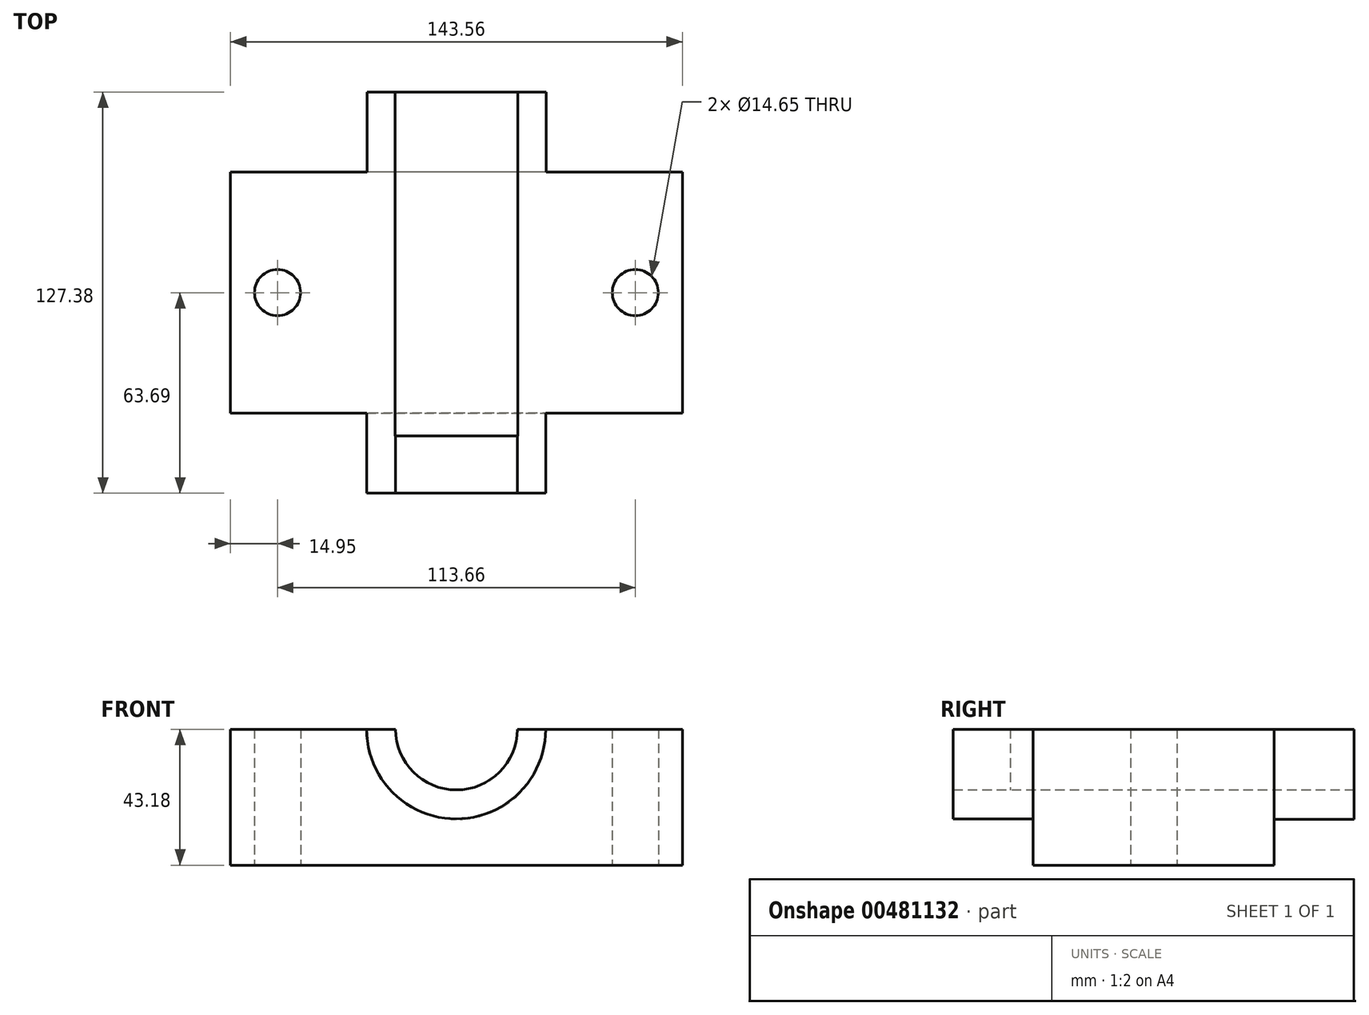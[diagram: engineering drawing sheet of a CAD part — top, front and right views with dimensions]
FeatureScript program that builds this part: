
annotation { "Feature Type Name" : "Feature", "Feature Type Description" : "" }
export const myFeature = defineFeature(function(context is Context, id is Id, definition is map)
    precondition{}
    {
        {
            var Q0;
            Q0=qCreatedBy(makeId("Top.planeOp"),FACE);
            var sketch = newSketch(context, id + "F0", { "sketchPlane" : qUnion([Q0])});
            skLineSegment(sketch, "E0.bottom", {"start": v(71.78, -38.29) * mm, "end": v(-71.78, -38.29) * mm});
            skLineSegment(sketch, "E0.top", {"start": v(71.78, 38.29) * mm, "end": v(-71.78, 38.29) * mm});
            skLineSegment(sketch, "E0.left", {"start": v(71.78, -38.29) * mm, "end": v(71.78, 38.29) * mm});
            skLineSegment(sketch, "E0.right", {"start": v(-71.78, -38.29) * mm, "end": v(-71.78, 38.29) * mm});
            skPoint(sketch, "E0.middle", {"position": v(0, 0) * mm});
            skCircle(sketch, "E1", {"center": v(-56.83, 0) * mm, "radius": 7.33 * mm});
            skCircle(sketch, "E2", {"center": v(56.83, 0) * mm, "radius": 7.33 * mm});
            skSolve(sketch);
        }
        {
            var Q0;
            Q0 = qSketchRegion(id + "F0", true);
            extrude(context, id + "F1", {"entities" : qUnion([Q0]), "depth" : 43.18 * mm});
        }
        {
            var Q0;
            Q0=makeQuery(id+"F1.opExtrude","SWEPT_FACE",FACE,{"disambiguationData":[OSD([sQuery(id+"F0.wireOp",EDGE,"E0.bottom")])]});
            var sketch = newSketch(context, id + "F2", { "sketchPlane" : qUnion([Q0])});
            skArc(sketch, "E3", {"start": v(-28.53, 43.18) * mm, "mid": v(-0.1, 14.7) * mm, "end": v(28.33, 43.18) * mm});
            skArc(sketch, "E4", {"start": v(-19.34, 43.18) * mm, "mid": v(0, 23.9) * mm, "end": v(19.34, 43.18) * mm});
            skSolve(sketch);
        }
        {
            var Q0;
            Q0 = qSketchRegion(id + "F2", true);
            var Q1;
            {var subQ0=sQuery(id+"F2.wireOp",EDGE,"E3");Q1=makeQuery(id+"F2.imprint","IMPRINT",FACE,{"disambiguationData":[TD([[makeQuery(id+"F2.imprint","IMPRINT",EDGE,{"derivedFrom":subQ0}),1.0]])]});}
            extrude(context, id + "F3", {"entities" : qUnion([Q0, Q1]), "operationType" : NewBodyOperationType.ADD, "depth" : 25.4 * mm});
        }
        {
            var Q0;
            Q0=makeQuery(id+"F1.opExtrude","SWEPT_FACE",FACE,{"disambiguationData":[OSD([sQuery(id+"F0.wireOp",EDGE,"E0.top")])]});
            var sketch = newSketch(context, id + "F4", { "sketchPlane" : qUnion([Q0])});
            skArc(sketch, "E5", {"start": v(-28.53, 43.18) * mm, "mid": v(-0.1, 14.54) * mm, "end": v(28.33, 43.18) * mm});
            skArc(sketch, "E6", {"start": v(-19.54, 43.18) * mm, "mid": v(0, 23.82) * mm, "end": v(19.54, 43.18) * mm});
            skSolve(sketch);
        }
        {
            var Q0;
            {var subQ0=sQuery(id+"F4.wireOp",EDGE,"E5");Q0=makeQuery(id+"F4.imprint","IMPRINT",FACE,{"disambiguationData":[TD([[makeQuery(id+"F4.imprint","IMPRINT",EDGE,{"derivedFrom":subQ0}),1.0]])]});}
            extrude(context, id + "F5", {"entities" : qUnion([Q0]), "operationType" : NewBodyOperationType.ADD, "depth" : 25.4 * mm});
        }
        {
            var Q0;
            {var subQ0=sQuery(id+"F4.wireOp",EDGE,"E6");var subQ5=sQuery(id+"F0.wireOp",EDGE,"E0.top");Q0=makeQuery(id+"F5.boolean.opBoolean","SPLIT",FACE,{"disambiguationData":[TD([makeQuery(id+"F5.opExtrude","SWEPT_FACE",FACE,{"disambiguationData":[OSD([subQ0])]})])],"derivedFrom":makeQuery(id+"F1.opExtrude","SWEPT_FACE",FACE,{"disambiguationData":[OSD([subQ5])]})});}
            extrude(context, id + "F6", {"entities" : qUnion([Q0]), "operationType" : NewBodyOperationType.REMOVE, "oppositeDirection" : true, "depth" : 83.82 * mm});
        }
    });
